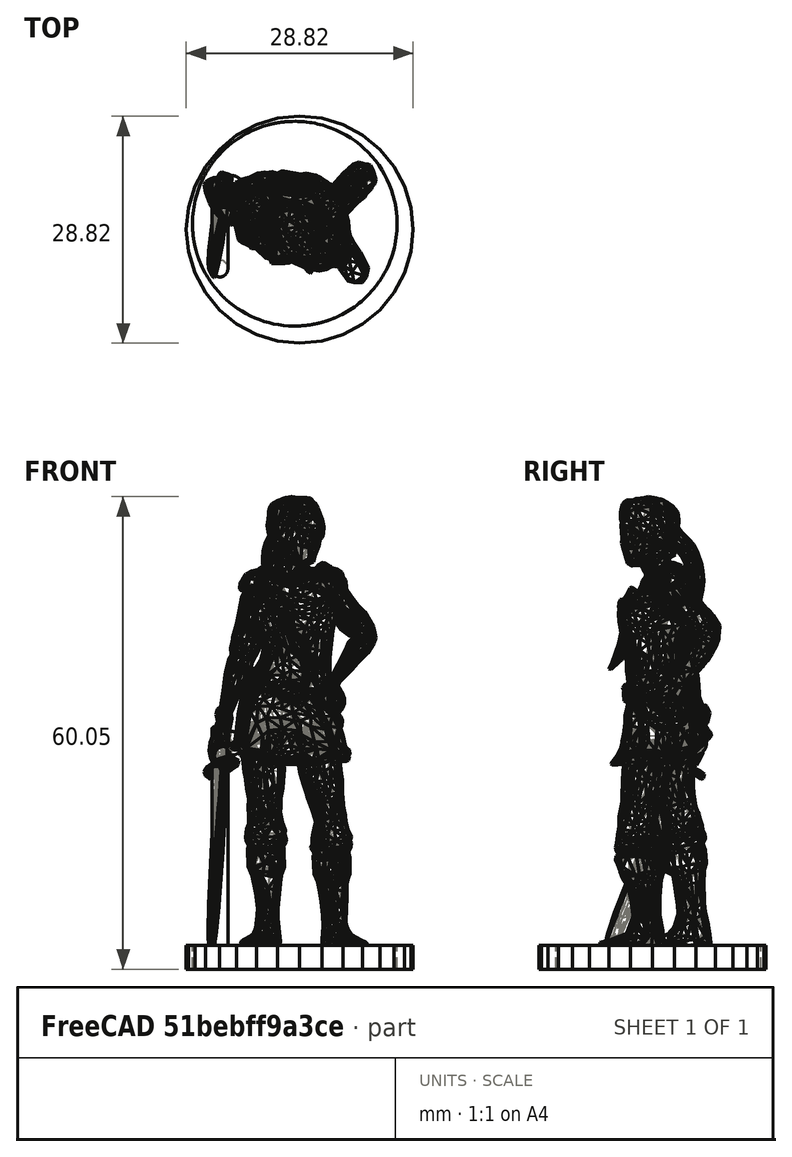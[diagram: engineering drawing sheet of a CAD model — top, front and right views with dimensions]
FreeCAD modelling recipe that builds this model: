
FCSTD DOCUMENT  (FreeCAD 0.18.1R)
Label: StandRelaxedFix0
License: All rights reserved
LicenseURL: http://en.wikipedia.org/wiki/All_rights_reserved
objects: Part::Feature×3, Part::Cylinder×3, Part::Cut×2, Part::Fuse×2, Mesh::Feature×1, Part::Sphere×1
note: 11 computed .brp shape members not serialized (recipe doc carries the construction recipe); baked Part::Feature solids carry a one-line shape summary decoded from their .brp

FEATURE [Mesh::Feature] FemaleKnight_StandRelaxed_Cleaned4
FEATURE [Part::Feature] FemaleKnight_StandRelaxed_Cleaned4001
  shape: bbox 28.82 x 28.82 x 60.05 mm, 8000 faces, 0 solids (baked)
FEATURE [Part::Feature] FemaleKnight_StandRelaxed_Cleaned4001_solid  label="FemaleKnight_StandRelaxed_Cleaned4001 (Solid)"
  shape: bbox 28.82 x 28.82 x 60.05 mm, 8000 faces (baked)
FEATURE [Part::Cylinder] Cylinder001
  Angle = 360
  AttacherType = Attacher::AttachEngine3D
  Height = 7
  Radius = 13
FEATURE [Part::Cylinder] Cylinder002
  Angle = 360
  AttacherType = Attacher::AttachEngine3D
  Height = 7
  Radius = 16
FEATURE [Part::Cut] Cut
  Base = -> Cylinder002
  Tool = -> Cylinder001
FEATURE [Part::Cut] Cut001
  Base = -> FemaleKnight_StandRelaxed_Cleaned4001_solid
  Tool = -> Cut
FEATURE [Part::Feature] FemaleKnight_StandRelaxed_Cleaned4001_solid001  label="FemaleKnight_StandRelaxed_Cleaned4001 (Solid)001"
  shape: bbox 28.82 x 28.82 x 60.05 mm, 8000 faces (baked)
FEATURE [Part::Cylinder] Cylinder
  Angle = 360
  AttacherType = Attacher::AttachEngine3D
  Height = 32
  Placement = pos=(-9.5,-6.6,1) rot=(-1,0,0;0.366519rad)
  Radius = 1
FEATURE [Part::Sphere] Sphere
  Angle1 = -90
  Angle2 = 90
  Angle3 = 360
  AttacherType = Attacher::AttachEngine3D
  Placement = pos=(-8,4.6,29) rot=(0,0,1;0rad)
  Radius = 1.5
FEATURE [Part::Fuse] Fusion
  Base = -> FemaleKnight_StandRelaxed_Cleaned4001_solid001
  Tool = -> Cylinder
FEATURE [Part::Fuse] Fusion001
  Base = -> Fusion
  Tool = -> Sphere
